# Revit family: 2-5-1_Sliding-Door_TX9200SL_Single-RH-Outside-Slide-SX-O_Tormax
name_source: partatom
category: Doors
units: mm (PartAtom-declared; Revit-internal decimal feet)

## family parameters
Always vertical = Yes
Classification Number = 23.30.10.00
Cut with Voids When Loaded = No
Host = Wall
Room Calculation Point = No
Shared = No

## types (3) — shared parameters
Analytic Construction = <None>
CAD Details = https://www.arcat.com
Define Thermal Properties by = Schematic Type
Door Height = 92"
Frame Material = Aluminum - Tormax
Frame Projection Ext. = 0"
Frame Projection Int. = 0"
Frame Width = 0"
Glass = Glass - Tormax
Height = 92"
Keynote = 08 42 29
Manufacturer = Tormax
Model = TX9200SL
Product Page URL = https://www.arcat.com
Rough Height = 92 1/4"
Specification = https://www.arcat.com
Thickness = 4 1/2"
URL = https://www.tormaxusa.com
Wall Closure = By host

## per-type parameters (varying)
| type | Description | Door Width | Rough Width | Width |
| 7'-0" Package Width | Single RH Outside Slide Application (SX-O), 7'-0" Package Width | 41 9/16" | 84 1/2" | 84" |
| 8'-0" Package Width | Single RH Outside Slide Application (SX-O), 8'-0" Package Width | 47 9/16" | 96 1/2" | 96" |
| 9'-0" Package Width | Single RH Outside Slide Application (SX-O), 9'-0" Package Width | 53 9/16" | 108 1/2" | 108" |

## geometry (parser evidence)
native form markers: Sweep x7
no freeform markers — native parametric forms only
